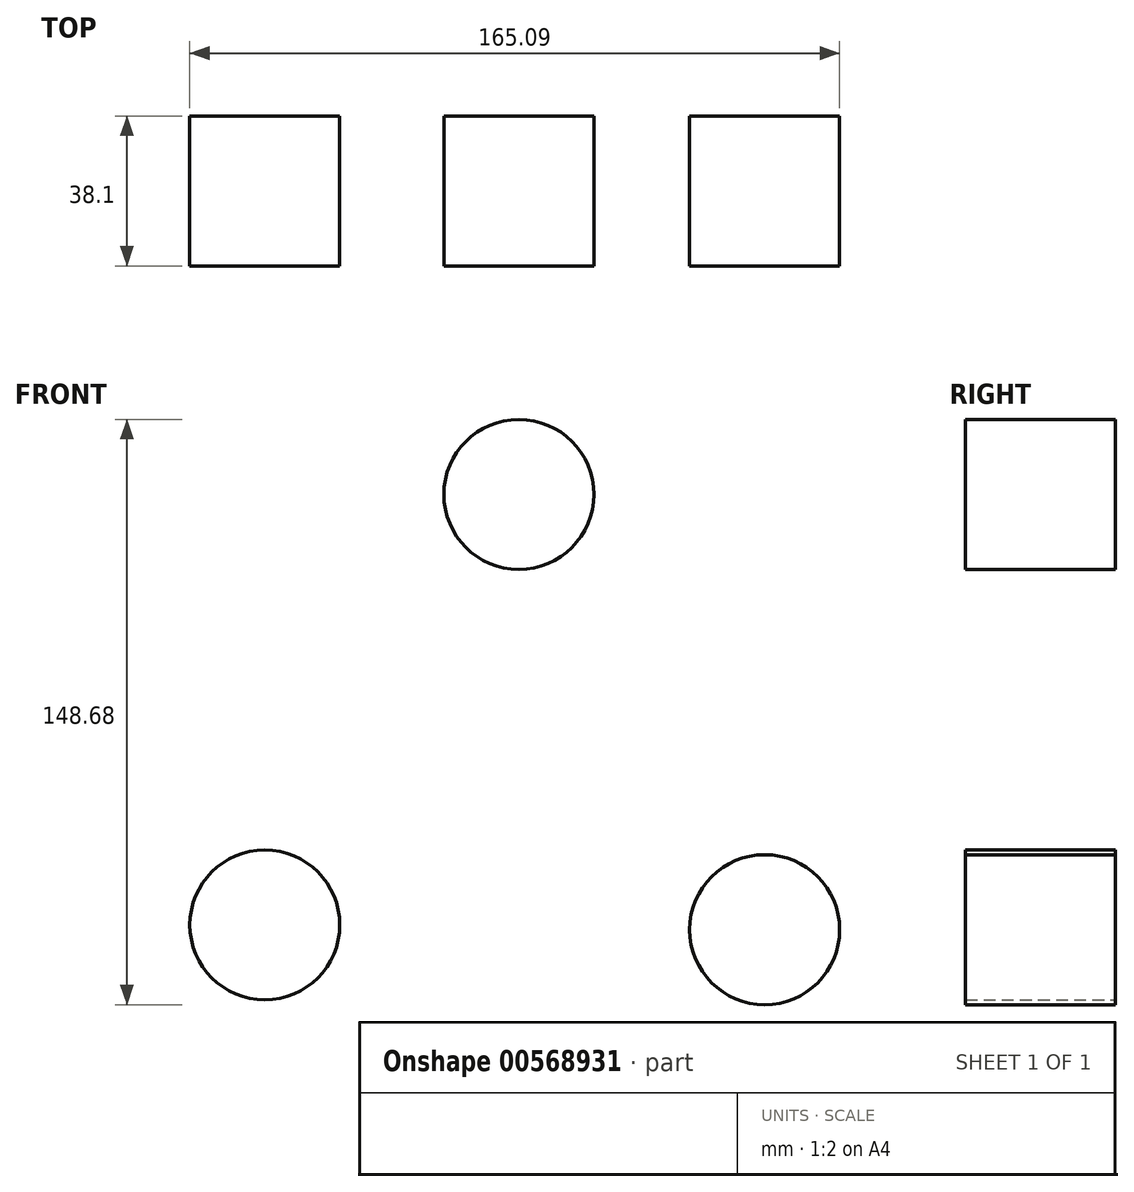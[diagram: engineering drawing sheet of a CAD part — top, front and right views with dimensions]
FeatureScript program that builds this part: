
annotation { "Feature Type Name" : "Feature", "Feature Type Description" : "" }
export const myFeature = defineFeature(function(context is Context, id is Id, definition is map)
    precondition{}
    {
        {
            var Q0;
            Q0=qCreatedBy(makeId("Front.planeOp"),FACE);
            var sketch = newSketch(context, id + "F0", { "sketchPlane" : qUnion([Q0])});
            skCircle(sketch, "E0", {"center": v(0, 76.3) * mm, "radius": 19.05 * mm});
            skCircle(sketch, "E1", {"center": v(-64.54, -33.07) * mm, "radius": 19.05 * mm});
            skCircle(sketch, "E2", {"center": v(62.45, -34.28) * mm, "radius": 19.05 * mm});
            skSolve(sketch);
        }
        {
            var Q0;
            Q0=makeQuery(id+"F0.imprint","IMPRINT",FACE,{"disambiguationData":[TD([[makeQuery(id+"F0.imprint","IMPRINT",EDGE,{"derivedFrom":sQuery(id+"F0.wireOp",EDGE,"E0")}),1.0]])]});
            var Q1;
            Q1=makeQuery(id+"F0.imprint","IMPRINT",FACE,{"disambiguationData":[TD([[makeQuery(id+"F0.imprint","IMPRINT",EDGE,{"derivedFrom":sQuery(id+"F0.wireOp",EDGE,"E1")}),1.0]])]});
            var Q2;
            Q2=makeQuery(id+"F0.imprint","IMPRINT",FACE,{"disambiguationData":[TD([[makeQuery(id+"F0.imprint","IMPRINT",EDGE,{"derivedFrom":sQuery(id+"F0.wireOp",EDGE,"E2")}),1.0]])]});
            extrude(context, id + "F1", {"entities" : qUnion([Q0, Q1, Q2]), "depth" : 38.1 * mm, "offsetDistance" : 25.4 * mm});
        }
    });
